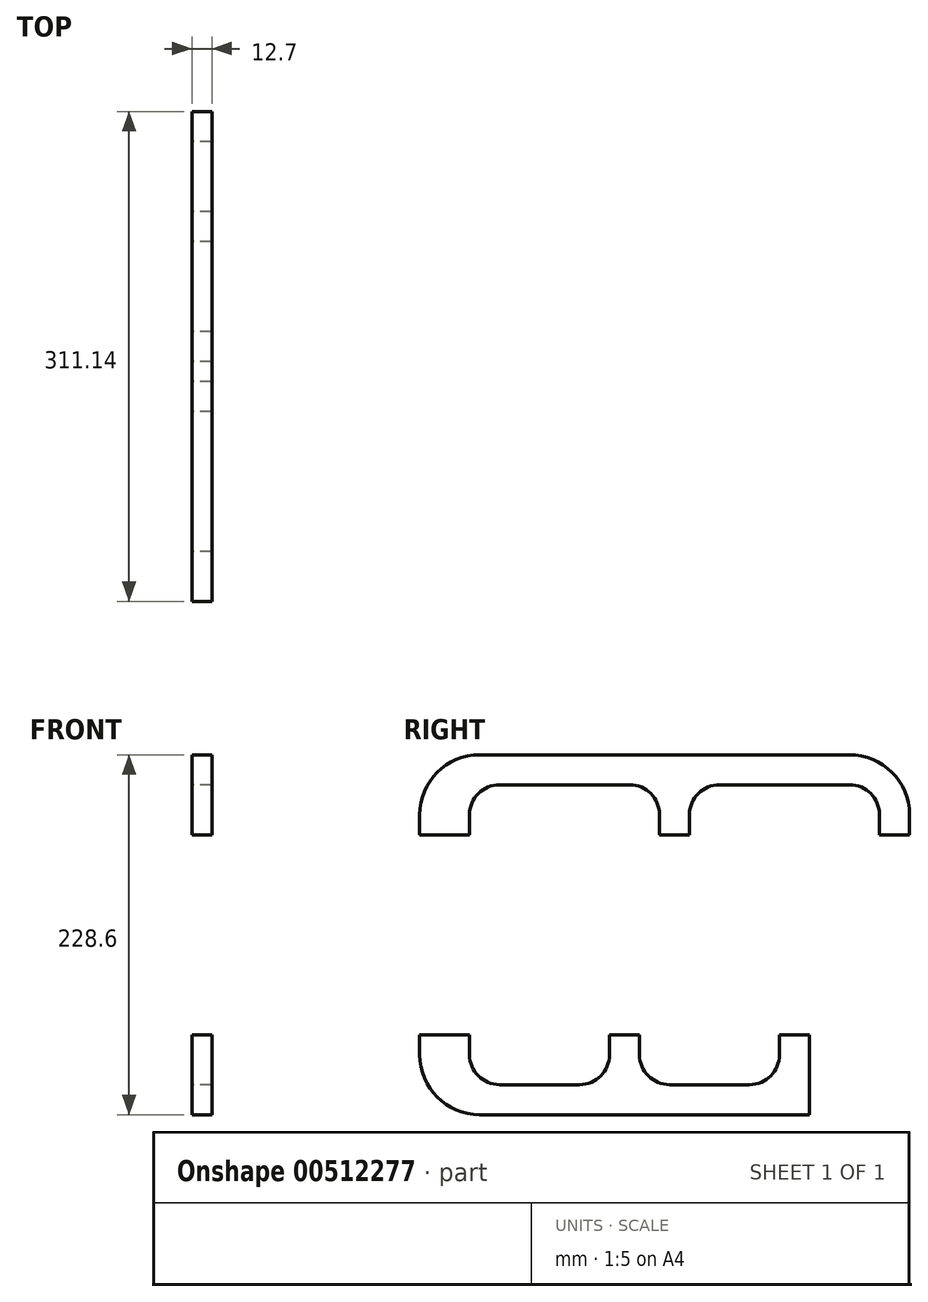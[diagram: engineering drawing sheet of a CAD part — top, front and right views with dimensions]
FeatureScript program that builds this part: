
annotation { "Feature Type Name" : "Feature", "Feature Type Description" : "" }
export const myFeature = defineFeature(function(context is Context, id is Id, definition is map)
    precondition{}
    {
        {
            var Q0;
            Q0=qCreatedBy(makeId("Right.planeOp"),FACE);
            var sketch = newSketch(context, id + "F0", { "sketchPlane" : qUnion([Q0])});
            skLineSegment(sketch, "E0", {"start": v(-155.58, 0) * mm, "end": v(-155.58, 12.7) * mm});
            skArc(sketch, "E1", {"start": v(-117.48, 50.8) * mm, "mid": v(-144.42, 39.64) * mm, "end": v(-155.58, 12.7) * mm});
            skLineSegment(sketch, "E2", {"start": v(-117.48, 50.8) * mm, "end": v(117.48, 50.8) * mm});
            skArc(sketch, "E3", {"start": v(155.58, 12.7) * mm, "mid": v(144.42, 39.64) * mm, "end": v(117.48, 50.8) * mm});
            skLineSegment(sketch, "E4", {"start": v(155.58, 12.7) * mm, "end": v(155.58, 0) * mm});
            skLineSegment(sketch, "E5", {"start": v(155.58, 0) * mm, "end": v(-155.58, 0) * mm});
            skLineSegment(sketch, "E6.0", {"start": v(-3.17, 12.7) * mm, "end": v(-3.17, 0) * mm});
            skArc(sketch, "E6.2", {"start": v(-104.78, 31.75) * mm, "mid": v(-118.25, 26.17) * mm, "end": v(-123.83, 12.7) * mm});
            skLineSegment(sketch, "E6.3", {"start": v(-104.78, 31.75) * mm, "end": v(-22.22, 31.75) * mm});
            skArc(sketch, "E6.4", {"start": v(-3.17, 12.7) * mm, "mid": v(-8.75, 26.17) * mm, "end": v(-22.22, 31.75) * mm});
            skLineSegment(sketch, "E7", {"start": v(-123.83, 12.7) * mm, "end": v(-123.83, 0) * mm});
            skLineSegment(sketch, "E8", {"start": v(15.88, 0) * mm, "end": v(15.88, 12.7) * mm});
            skLineSegment(sketch, "E9", {"start": v(34.92, 31.75) * mm, "end": v(117.48, 31.75) * mm});
            skLineSegment(sketch, "E10", {"start": v(136.52, 0) * mm, "end": v(136.52, 12.7) * mm});
            skArc(sketch, "E11", {"start": v(34.92, 31.75) * mm, "mid": v(21.45, 26.17) * mm, "end": v(15.88, 12.7) * mm});
            skArc(sketch, "E12", {"start": v(136.52, 12.7) * mm, "mid": v(130.95, 26.17) * mm, "end": v(117.48, 31.75) * mm});
            skLineSegment(sketch, "E13", {"start": v(-155.58, -127) * mm, "end": v(-155.58, -139.7) * mm});
            skLineSegment(sketch, "E14", {"start": v(-117.47, -177.8) * mm, "end": v(92.08, -177.8) * mm});
            skLineSegment(sketch, "E15", {"start": v(92.08, -177.8) * mm, "end": v(92.08, -127) * mm});
            skLineSegment(sketch, "E16", {"start": v(92.08, -127) * mm, "end": v(-155.58, -127) * mm});
            skArc(sketch, "E17", {"start": v(-155.57, -139.7) * mm, "mid": v(-144.42, -166.64) * mm, "end": v(-117.47, -177.8) * mm});
            skLineSegment(sketch, "E18", {"start": v(-123.83, -127) * mm, "end": v(-123.83, -139.7) * mm});
            skLineSegment(sketch, "E19", {"start": v(-104.78, -158.75) * mm, "end": v(-53.97, -158.75) * mm});
            skLineSegment(sketch, "E20", {"start": v(3.17, -158.75) * mm, "end": v(53.98, -158.75) * mm});
            skLineSegment(sketch, "E21", {"start": v(73.03, -139.7) * mm, "end": v(73.03, -127) * mm});
            skArc(sketch, "E22", {"start": v(-123.83, -139.7) * mm, "mid": v(-118.25, -153.17) * mm, "end": v(-104.78, -158.75) * mm});
            skArc(sketch, "E23", {"start": v(-53.97, -158.75) * mm, "mid": v(-40.5, -153.17) * mm, "end": v(-34.92, -139.7) * mm});
            skArc(sketch, "E24", {"start": v(53.98, -158.75) * mm, "mid": v(67.45, -153.17) * mm, "end": v(73.03, -139.7) * mm});
            skArc(sketch, "E25", {"start": v(-15.88, -139.7) * mm, "mid": v(-10.3, -153.17) * mm, "end": v(3.17, -158.75) * mm});
            skLineSegment(sketch, "E26", {"start": v(-34.92, -139.7) * mm, "end": v(-34.92, -127) * mm});
            skLineSegment(sketch, "E27", {"start": v(-15.88, -139.7) * mm, "end": v(-15.88, -127) * mm});
            skSolve(sketch);
        }
        {
            var Q0;
            {var subQ2=sQuery(id+"F0.wireOp",EDGE,"E0");Q0=makeQuery(id+"F0.imprint","IMPRINT",FACE,{"disambiguationData":[TD([[makeQuery(id+"F0.imprint","IMPRINT",EDGE,{"derivedFrom":subQ2}),-1.0]])]});}
            extrude(context, id + "F1", {"entities" : qUnion([Q0]), "depth" : 12.7 * mm});
        }
        {
            var Q0;
            {var subQ2=sQuery(id+"F0.wireOp",EDGE,"E13");Q0=makeQuery(id+"F0.imprint","IMPRINT",FACE,{"disambiguationData":[TD([[makeQuery(id+"F0.imprint","IMPRINT",EDGE,{"derivedFrom":subQ2}),1.0]])]});}
            extrude(context, id + "F2", {"entities" : qUnion([Q0]), "depth" : 12.7 * mm});
        }
    });
